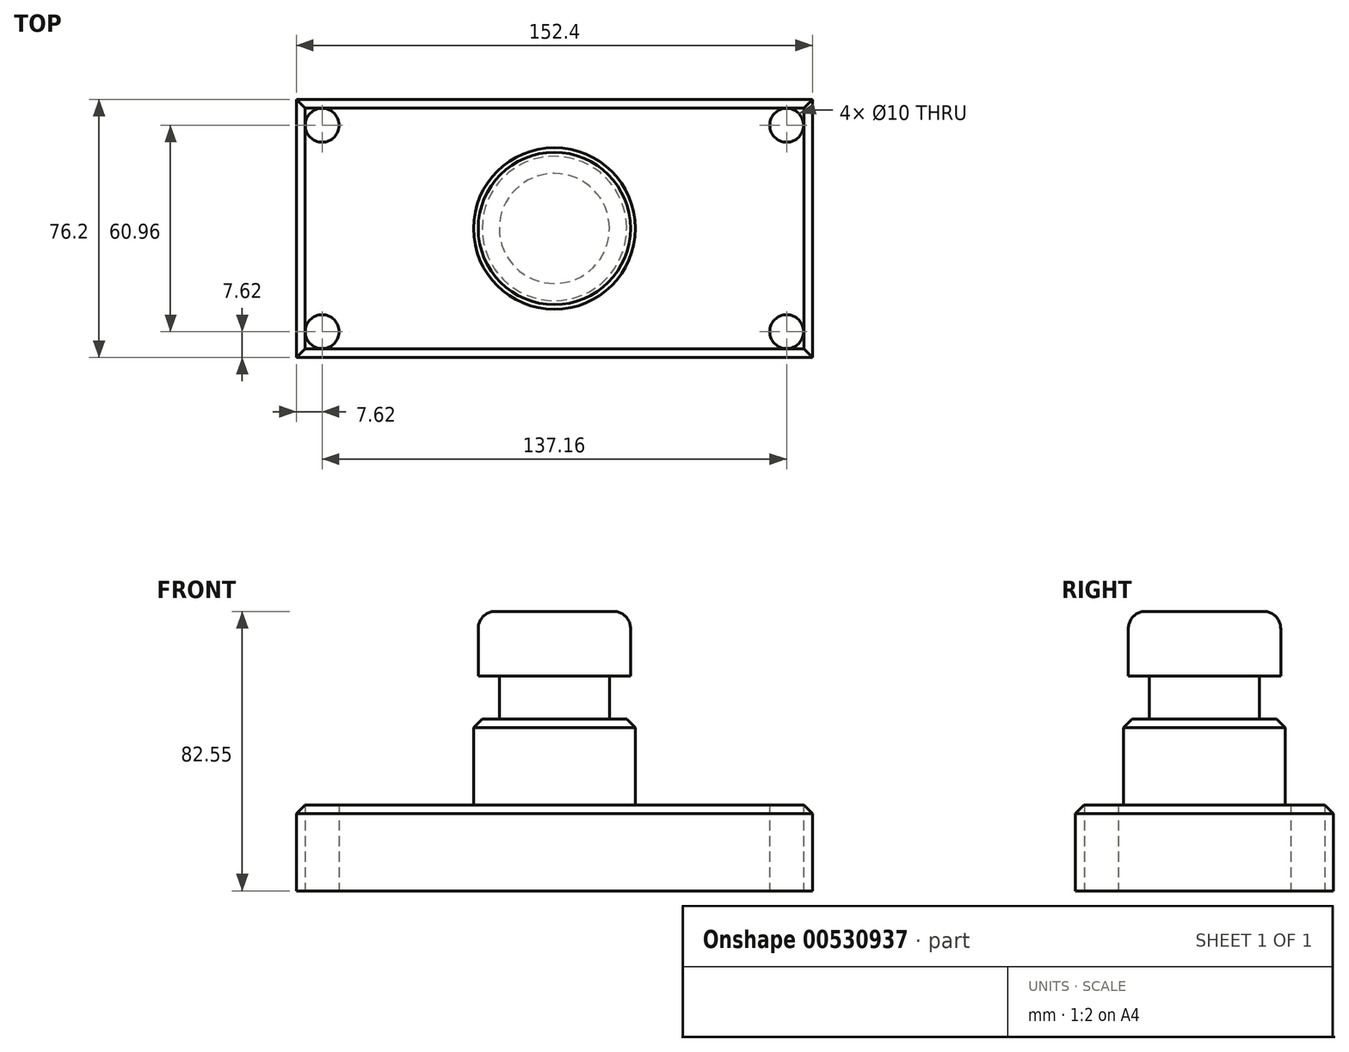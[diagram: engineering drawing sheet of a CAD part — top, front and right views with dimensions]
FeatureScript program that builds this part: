
annotation { "Feature Type Name" : "Feature", "Feature Type Description" : "" }
export const myFeature = defineFeature(function(context is Context, id is Id, definition is map)
    precondition{}
    {
        {
            var Q0;
            Q0=qCreatedBy(makeId("Top.planeOp"),FACE);
            var sketch = newSketch(context, id + "F0", { "sketchPlane" : qUnion([Q0])});
            skLineSegment(sketch, "E0.bottom", {"start": v(-76.2, 38.1) * mm, "end": v(76.2, 38.1) * mm});
            skLineSegment(sketch, "E0.top", {"start": v(-76.2, -38.1) * mm, "end": v(76.2, -38.1) * mm});
            skLineSegment(sketch, "E0.left", {"start": v(-76.2, 38.1) * mm, "end": v(-76.2, -38.1) * mm});
            skLineSegment(sketch, "E0.right", {"start": v(76.2, 38.1) * mm, "end": v(76.2, -38.1) * mm});
            skPoint(sketch, "E0.middle", {"position": v(0, 0) * mm});
            skCircle(sketch, "E1", {"center": v(-68.58, 30.48) * mm, "radius": 5 * mm});
            skCircle(sketch, "E2", {"center": v(68.58, -30.48) * mm, "radius": 5 * mm});
            skCircle(sketch, "E3", {"center": v(68.58, 30.48) * mm, "radius": 5 * mm});
            skCircle(sketch, "E4", {"center": v(-68.58, -30.48) * mm, "radius": 5 * mm});
            skSolve(sketch);
        }
        {
            var Q0;
            Q0=makeQuery(id+"F0.imprint","IMPRINT",FACE,{"disambiguationData":[TD([[makeQuery(id+"F0.imprint","IMPRINT",EDGE,{"derivedFrom":sQuery(id+"F0.wireOp",EDGE,"E0.bottom")}),-1.0]])]});
            extrude(context, id + "F1", {"entities" : qUnion([Q0]), "depth" : 25.4 * mm, "offsetDistance" : 25.4 * mm});
        }
        {
            var Q0;
            Q0=makeQuery(id+"F1.opExtrude","CAP_FACE",FACE,{"disambiguationData":[OSD([sQuery(id+"F0.wireOp",EDGE,"E0.bottom"),sQuery(id+"F0.wireOp",EDGE,"E0.top"),sQuery(id+"F0.wireOp",EDGE,"E0.left"),sQuery(id+"F0.wireOp",EDGE,"E0.right"),sQuery(id+"F0.wireOp",EDGE,"E1"),sQuery(id+"F0.wireOp",EDGE,"E2"),sQuery(id+"F0.wireOp",EDGE,"E3"),sQuery(id+"F0.wireOp",EDGE,"E4")])],"isStart":false});
            var sketch = newSketch(context, id + "F2", { "sketchPlane" : qUnion([Q0])});
            skCircle(sketch, "E5", {"center": v(0, 0) * mm, "radius": 23.87 * mm});
            skSolve(sketch);
        }
        {
            var Q0;
            Q0=makeQuery(id+"F2.imprint","IMPRINT",FACE,{"disambiguationData":[TD([[makeQuery(id+"F2.imprint","IMPRINT",EDGE,{"derivedFrom":sQuery(id+"F2.wireOp",EDGE,"E5")}),1.0]])]});
            var Q1;
            Q1=sQuery(id+"F2.wireOp",EDGE,"E5");
            extrude(context, id + "F3", {"entities" : qUnion([Q0]), "surfaceEntities" : qUnion([Q1]), "depth" : 25.4 * mm, "offsetDistance" : 25.4 * mm});
        }
        {
            var Q0;
            Q0=makeQuery(id+"F3.opExtrude","CAP_FACE",FACE,{"disambiguationData":[OSD([sQuery(id+"F2.wireOp",EDGE,"E5")])],"isStart":false});
            var sketch = newSketch(context, id + "F4", { "sketchPlane" : qUnion([Q0])});
            skCircle(sketch, "E6", {"center": v(0, 0) * mm, "radius": 16.25 * mm});
            skSolve(sketch);
        }
        {
            var Q0;
            Q0 = qSketchRegion(id + "F4", true);
            extrude(context, id + "F5", {"entities" : qUnion([Q0]), "operationType" : NewBodyOperationType.ADD, "depth" : 12.7 * mm, "offsetDistance" : 25.4 * mm});
        }
        {
            var Q0;
            Q0=makeQuery(id+"F5.opExtrude","CAP_FACE",FACE,{"disambiguationData":[OSD([sQuery(id+"F4.wireOp",EDGE,"E6")])],"isStart":false});
            var sketch = newSketch(context, id + "F6", { "sketchPlane" : qUnion([Q0])});
            skCircle(sketch, "E7", {"center": v(0, 0) * mm, "radius": 22.5 * mm});
            skSolve(sketch);
        }
        {
            var Q0;
            Q0 = qSketchRegion(id + "F6", true);
            extrude(context, id + "F7", {"entities" : qUnion([Q0]), "operationType" : NewBodyOperationType.ADD, "depth" : 19.05 * mm, "offsetDistance" : 25.4 * mm});
        }
        {
            var Q0;
            Q0=makeQuery(id+"F1.opExtrude","CAP_EDGE",EDGE,{"disambiguationData":[OSD([sQuery(id+"F0.wireOp",EDGE,"E0.top")])],"isStart":false});
            var Q1;
            Q1=makeQuery(id+"F1.opExtrude","CAP_EDGE",EDGE,{"disambiguationData":[OSD([sQuery(id+"F0.wireOp",EDGE,"E0.right")])],"isStart":false});
            var Q2;
            Q2=makeQuery(id+"F1.opExtrude","CAP_EDGE",EDGE,{"disambiguationData":[OSD([sQuery(id+"F0.wireOp",EDGE,"E0.left")])],"isStart":false});
            var Q3;
            Q3=makeQuery(id+"F1.opExtrude","CAP_EDGE",EDGE,{"disambiguationData":[OSD([sQuery(id+"F0.wireOp",EDGE,"E0.bottom")])],"isStart":false});
            var Q4;
            Q4=makeQuery(id+"F3.opExtrude","CAP_EDGE",EDGE,{"disambiguationData":[OSD([sQuery(id+"F2.wireOp",EDGE,"E5")])],"isStart":false});
            chamfer(context, id + "F8", {"entities" : qUnion([Q0, Q1, Q2, Q3, Q4]), "width" : 2.54 * mm, "tangentPropagation" : true});
        }
        {
            var Q0;
            Q0=makeQuery(id+"F7.opExtrude","CAP_EDGE",EDGE,{"disambiguationData":[OSD([sQuery(id+"F6.wireOp",EDGE,"E7")])],"isStart":false});
            fillet(context, id + "F9", {"entities" : qUnion([Q0]), "radius" : 5.08 * mm, "tangentPropagation" : true, "allowEdgeOverflow" : false});
        }
    });
